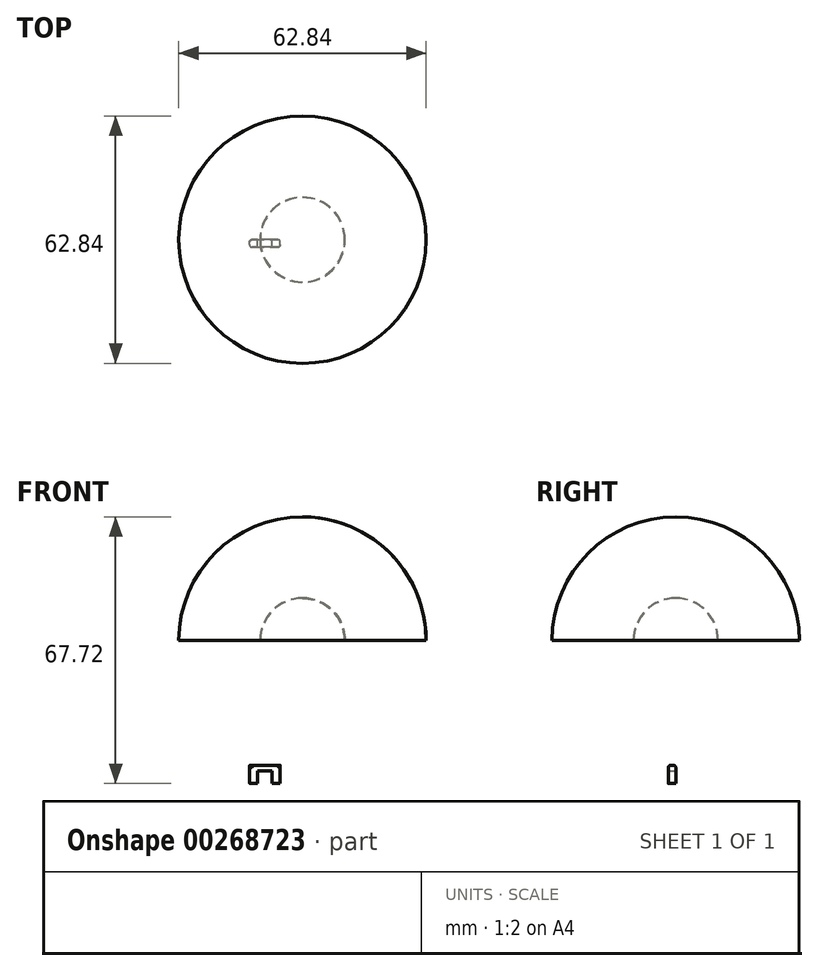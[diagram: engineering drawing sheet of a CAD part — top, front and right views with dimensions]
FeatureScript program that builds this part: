
annotation { "Feature Type Name" : "Feature", "Feature Type Description" : "" }
export const myFeature = defineFeature(function(context is Context, id is Id, definition is map)
    precondition{}
    {
        {
            var Q0;
            Q0=qCreatedBy(makeId("Front.planeOp"),FACE);
            var sketch = newSketch(context, id + "F0", { "sketchPlane" : qUnion([Q0])});
            skArc(sketch, "E0", {"start": v(0, 31.42) * mm, "mid": v(-22.22, 22.22) * mm, "end": v(-31.42, 0) * mm});
            skLineSegment(sketch, "E1", {"start": v(0, 0) * mm, "end": v(0, 31.42) * mm});
            skLineSegment(sketch, "E2", {"start": v(0, 31.42) * mm, "end": v(0, -31.42) * mm});
            skLineSegment(sketch, "E3", {"start": v(0, -31.42) * mm, "end": v(0, 0) * mm});
            skLineSegment(sketch, "E4", {"start": v(31.42, 0) * mm, "end": v(-31.42, 0) * mm});
            skSolve(sketch);
        }
        {
            var Q0;
            {var subQ0=sQuery(id+"F0.wireOp",EDGE,"E0");Q0=makeQuery(id+"F0.imprint","IMPRINT",FACE,{"disambiguationData":[TD([[makeQuery(id+"F0.imprint","IMPRINT",EDGE,{"derivedFrom":subQ0}),1.0]])]});}
            var Q1;
            Q1=sQuery(id+"F0.wireOp",EDGE,"E2");
            revolve(context, id + "F1", {"entities" : qUnion([Q0]), "axis" : qUnion([Q1]), "revolveType" : RevolveType.FULL});
        }
        {
            var Q0;
            Q0=makeQuery(id+"F1.opRevolve","SWEPT_FACE",FACE,{"disambiguationData":[OSD([sQuery(id+"F0.wireOp",EDGE,"E4")])]});
            shell(context, id + "F2", {"entities" : qUnion([Q0]), "thickness" : 0.13 * mm});
        }
        {
            var Q0;
            Q0=qCreatedBy(makeId("Front.planeOp"),FACE);
            var sketch = newSketch(context, id + "F3", { "sketchPlane" : qUnion([Q0])});
            skArc(sketch, "E5", {"start": v(10.83, 0) * mm, "mid": v(7.66, 7.66) * mm, "end": v(0, 10.83) * mm});
            skLineSegment(sketch, "E6", {"start": v(0, 0) * mm, "end": v(0, 10.83) * mm});
            skLineSegment(sketch, "E7", {"start": v(0, 0) * mm, "end": v(10.83, 0) * mm});
            skSolve(sketch);
        }
        {
            var Q0;
            Q0=makeQuery(id+"F3.imprint","IMPRINT",FACE,{"disambiguationData":[TD([[makeQuery(id+"F3.imprint","IMPRINT",EDGE,{"derivedFrom":sQuery(id+"F3.wireOp",EDGE,"E5")}),1.0]])]});
            var Q1;
            Q1=sQuery(id+"F3.wireOp",EDGE,"E6");
            revolve(context, id + "F4", {"entities" : qUnion([Q0]), "axis" : qUnion([Q1]), "revolveType" : RevolveType.FULL});
        }
        {
            var Q0;
            Q0=makeQuery(id+"F4.opRevolve","SWEPT_FACE",FACE,{"disambiguationData":[OSD([sQuery(id+"F3.wireOp",EDGE,"E7")])]});
            shell(context, id + "F5", {"entities" : qUnion([Q0]), "thickness" : 0.13 * mm});
        }
        {
            var Q0;
            Q0=qCreatedBy(makeId("Front.planeOp"),FACE);
            var sketch = newSketch(context, id + "F6", { "sketchPlane" : qUnion([Q0])});
            skCircle(sketch, "E8", {"center": v(-49.01, 40.58) * mm, "radius": 11.1 * mm});
            skArc(sketch, "E9", {"start": v(37.22, 52.9) * mm, "mid": v(31.1, 34.94) * mm, "end": v(49.04, 41.08) * mm});
            skSolve(sketch);
        }
        {
            var Q0;
            Q0=sQuery(id+"F6.wireOp",EDGE,"E8");
            extrude(context, id + "F7", {"bodyType" : ToolBodyType.SURFACE, "surfaceEntities" : qUnion([Q0]), "oppositeDirection" : true, "depth" : 0.03 * mm});
        }
        {
            var Q0;
            Q0=qCreatedBy(makeId("Front.planeOp"),FACE);
            var sketch = newSketch(context, id + "F8", { "sketchPlane" : qUnion([Q0])});
            skLineSegment(sketch, "E10", {"start": v(-13.43, -36.3) * mm, "end": v(-13.43, -31.66) * mm});
            skLineSegment(sketch, "E11", {"start": v(-13.43, -31.66) * mm, "end": v(-5.64, -31.66) * mm});
            skLineSegment(sketch, "E12", {"start": v(-5.64, -31.66) * mm, "end": v(-5.64, -36.3) * mm});
            skLineSegment(sketch, "E13", {"start": v(-5.64, -36.3) * mm, "end": v(-7.75, -36.3) * mm});
            skLineSegment(sketch, "E14", {"start": v(-7.75, -36.3) * mm, "end": v(-7.75, -33.18) * mm});
            skLineSegment(sketch, "E15", {"start": v(-7.75, -33.18) * mm, "end": v(-11.37, -33.18) * mm});
            skLineSegment(sketch, "E16", {"start": v(-11.37, -33.18) * mm, "end": v(-11.37, -36.3) * mm});
            skLineSegment(sketch, "E17", {"start": v(-11.37, -36.3) * mm, "end": v(-13.43, -36.3) * mm});
            skSolve(sketch);
        }
        {
            var Q0;
            Q0=makeQuery(id+"F8.imprint","IMPRINT",FACE,{"disambiguationData":[TD([[makeQuery(id+"F8.imprint","IMPRINT",EDGE,{"derivedFrom":sQuery(id+"F8.wireOp",EDGE,"E10")}),-1.0]])]});
            extrude(context, id + "F9", {"entities" : qUnion([Q0]), "depth" : 1.9 * mm});
        }
        {
            var Q0;
            Q0=makeQuery(id+"F9.opExtrude","CAP_EDGE",EDGE,{"disambiguationData":[OSD([sQuery(id+"F8.wireOp",EDGE,"E11")])],"isStart":false});
            var Q1;
            Q1=makeQuery(id+"F9.opExtrude","CAP_EDGE",EDGE,{"disambiguationData":[OSD([sQuery(id+"F8.wireOp",EDGE,"E11")])],"isStart":true});
            var Q2;
            Q2=makeQuery(id+"F9.opExtrude","CAP_EDGE",EDGE,{"disambiguationData":[OSD([sQuery(id+"F8.wireOp",EDGE,"E12")])],"isStart":false});
            var Q3;
            Q3=makeQuery(id+"F9.opExtrude","CAP_EDGE",EDGE,{"disambiguationData":[OSD([sQuery(id+"F8.wireOp",EDGE,"E12")])],"isStart":true});
            var Q4;
            Q4=makeQuery(id+"F9.opExtrude","CAP_EDGE",EDGE,{"disambiguationData":[OSD([sQuery(id+"F8.wireOp",EDGE,"E10")])],"isStart":true});
            var Q5;
            Q5=makeQuery(id+"F9.opExtrude","CAP_EDGE",EDGE,{"disambiguationData":[OSD([sQuery(id+"F8.wireOp",EDGE,"E10")])],"isStart":false});
            fillet(context, id + "F10", {"entities" : qUnion([Q0, Q1, Q2, Q3, Q4, Q5]), "radius" : 0.64 * mm, "tangentPropagation" : true, "allowEdgeOverflow" : false});
        }
    });
